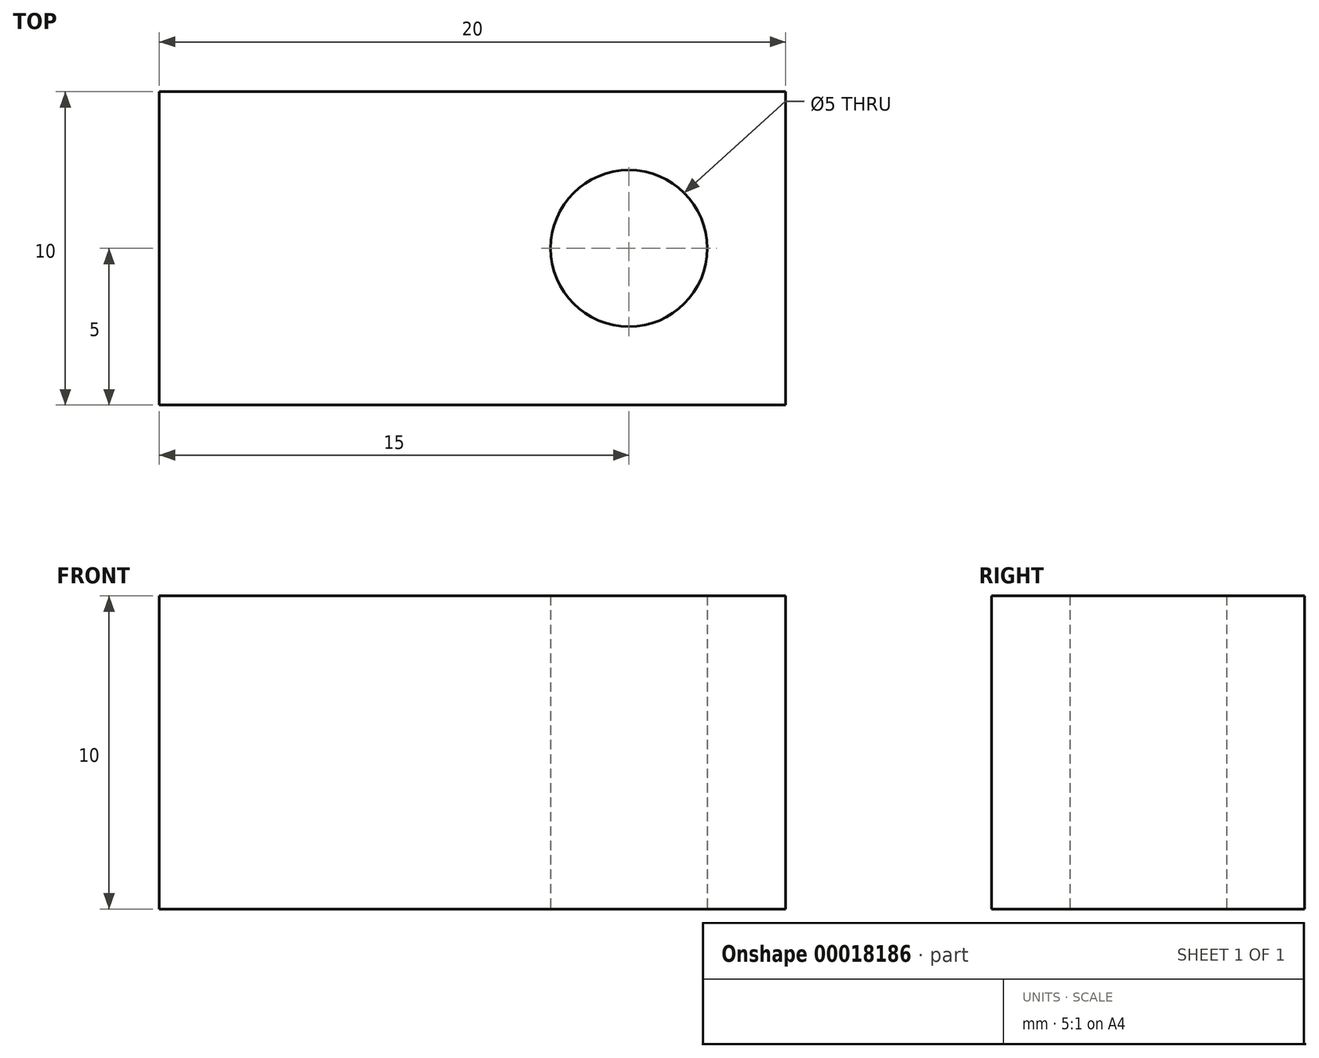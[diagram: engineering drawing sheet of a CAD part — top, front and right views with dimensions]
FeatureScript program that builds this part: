
annotation { "Feature Type Name" : "Feature", "Feature Type Description" : "" }
export const myFeature = defineFeature(function(context is Context, id is Id, definition is map)
    precondition{}
    {
        {
            var Q0;
            Q0=qCreatedBy(makeId("Top.planeOp"),FACE);
            var sketch = newSketch(context, id + "F0", { "sketchPlane" : qUnion([Q0])});
            skLineSegment(sketch, "E0.bottom", {"start": v(0, 0) * mm, "end": v(-20, 0) * mm});
            skLineSegment(sketch, "E0.top", {"start": v(0, -10) * mm, "end": v(-20, -10) * mm});
            skLineSegment(sketch, "E0.left", {"start": v(0, 0) * mm, "end": v(0, -10) * mm});
            skLineSegment(sketch, "E0.right", {"start": v(-20, 0) * mm, "end": v(-20, -10) * mm});
            skCircle(sketch, "E1", {"center": v(-5, -5) * mm, "radius": 2.5 * mm});
            skLineSegment(sketch, "E2", {"start": v(-20.87, -5) * mm, "end": v(3.54, -5) * mm, "construction": true});
            skLineSegment(sketch, "E3", {"start": v(-5, 1.26) * mm, "end": v(-5, -11.5) * mm, "construction": true});
            skSolve(sketch);
        }
        {
            var Q0;
            Q0=makeQuery(id+"F0.imprint","IMPRINT",FACE,{"disambiguationData":[TD([[makeQuery(id+"F0.imprint","IMPRINT",EDGE,{"derivedFrom":sQuery(id+"F0.wireOp",EDGE,"E0.bottom")}),1.0]])]});
            extrude(context, id + "F1", {"entities" : qUnion([Q0]), "depth" : 10 * mm});
        }
    });
